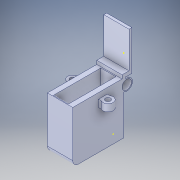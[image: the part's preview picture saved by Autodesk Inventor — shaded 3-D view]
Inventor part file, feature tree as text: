
AUTODESK INVENTOR PART (.ipt)
format: ipt  version: 2018 (Build 220112000, 112)  size: 337,920 bytes
history: native  units: in
note: dims shown in document units (in); Inventor stores cm internally (conversion verified against a paired STEP export)
features: sketch x22, extrude x18, fillet x4, other x1
ambient origin geometry x8: Origin, YZ Plane, XZ Plane, XY Plane, X Axis, Y Axis, Z Axis, Center Point
bodies: Solid1 (feature_tree)
feature tree (45):
  sketch  "Sketch1"  dims[d0=0.5906in d1=0.0in d2=0.3937in d3=0.0in]
  extrude  "Extrusion1"  Depth=0.3937in TaperAngle=0.0deg
  extrude  "Extrusion2"  Depth=0.4724in TaperAngle=0.0deg
  sketch  "Sketch4"  dims[d10=2.6378in d11=0.0in d12=0.315in]
  extrude  "Extrusion3"  Depth=0.2756in
  extrude  "Extrusion4"  Depth=0.315in
  extrude  "Extrusion5"  Depth=0.2756in
  fillet  "Fillet1"  Radius=0.2756in
  extrude  "Extrusion6"  Depth=1.1417in TaperAngle=0.0deg
  extrude  "Extrusion7"  Depth=0.315in
  sketch  "Sketch10"  dims[d31=0.5906in d32=0.0in d33=0.315in d34=0.0in]
  extrude  "Extrusion8"  Depth=0.315in
  fillet  "Fillet2"  Radius=0.5512in
  extrude  "Extrusion9"  Depth=0.2756in
  fillet  "Fillet3"  Radius=0.2756in
  extrude  "Extrusion10"  Depth=0.315in TaperAngle=0.0deg
  extrude  "Extrusion11"  Depth=0.1181in
  sketch  "3D Sketch1"
  extrude  "Extrusion12"  Depth=0.0787in TaperAngle=0.0deg
  extrude  "Extrusion14"  Depth=0.5512in
  extrude  "Extrusion15"  Depth=0.315in TaperAngle=0.0deg
  fillet  "Fillet4"  Radius=0.1181in
  extrude  "Extrusion16"  Depth=0.0787in TaperAngle=0.0deg
  extrude  "Extrusion17"  [1 undecoded]
  extrude  "Extrusion18"  [1 undecoded]
  extrude  "Extrusion19"  [1 undecoded]
  sketch  "Sketch2"  dims[d4=0.9843in d5=0.0in d6=0.4724in d7=0.0in]
  sketch  "Sketch3"  dims[d8=0.2756in d9=0.2756in]
  sketch  "Sketch5"  dims[d13=0.1969in d14=0.0in d15=0.2756in d16=0.2756in]
  sketch  "Sketch6"  dims[d18=1.3386in d19=1.1417in d20=0.0in]
  sketch  "Sketch7"  dims[d21=0.315in d22=0.0in d23=0.315in]
  sketch  "Sketch8"  dims[d24=0.1181in d25=0.0in d26=0.315in d27=0.5512in]
  sketch  "Sketch9"  dims[d28=0.5512in d29=0.2756in d30=0.2756in]
  sketch  "Sketch11"  dims[d36=0.3937in d37=0.0in d38=0.1181in]
  sketch  "Sketch12"  dims[d41=0.3937in d42=0.0in d43=0.0787in d44=0.0in]
  sketch  "Sketch14"  dims[d45=0.0787in d46=0.5512in]
  sketch  "Sketch15"  dims[d47=0.5512in d48=0.315in d49=0.0in d50=0.1181in d51=0.0in]
  sketch  "Sketch16"  dims[d52=0.0787in d53=0.1181in d54=0.0in d55=0.0in d56=0.0787in d57=0.0in]
  sketch  "Sketch17"
  sketch  "Sketch18"
  sketch  "Sketch19"
  sketch  "Sketch20"
  sketch  "Sketch21"
  sketch  "Sketch22"
  other  "Boss-Extrude7"
note: 3 required parameter values undecoded (feature->parameter linkage not recoverable at this tier; creation-order binding heuristic only, values carry confidence <= 0.55)
